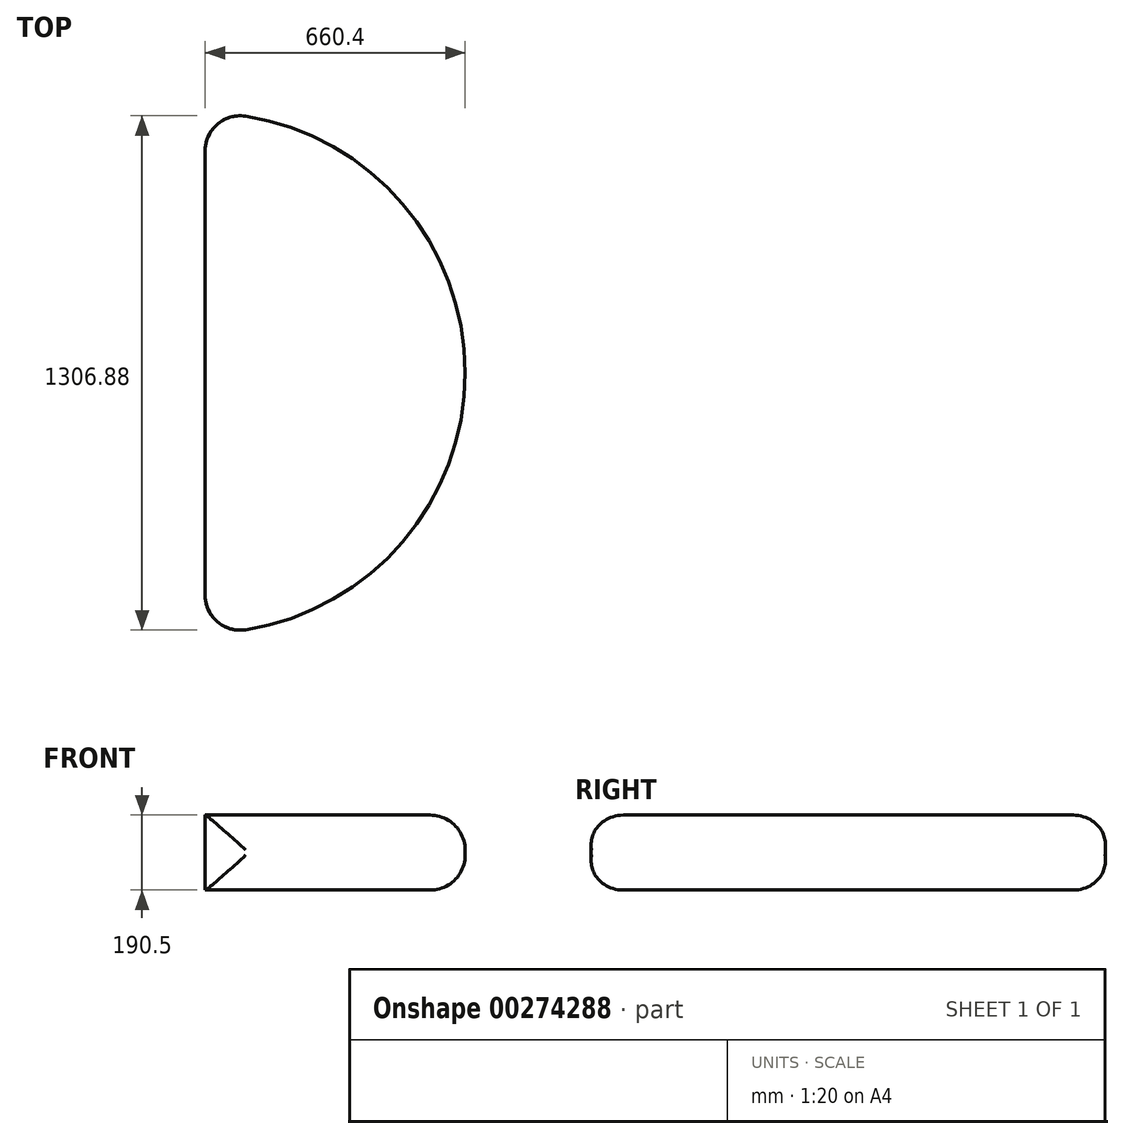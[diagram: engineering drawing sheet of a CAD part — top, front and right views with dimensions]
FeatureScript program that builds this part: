
annotation { "Feature Type Name" : "Feature", "Feature Type Description" : "" }
export const myFeature = defineFeature(function(context is Context, id is Id, definition is map)
    precondition{}
    {
        {
            var Q0;
            Q0=qCreatedBy(makeId("Top.planeOp"),FACE);
            var sketch = newSketch(context, id + "F0", { "sketchPlane" : qUnion([Q0])});
            skLineSegment(sketch, "E0", {"start": v(0, 0) * mm, "end": v(0, 660.4) * mm});
            skArc(sketch, "E1", {"start": v(0, 660.4) * mm, "mid": v(660.4, 0) * mm, "end": v(0, -660.4) * mm});
            skLineSegment(sketch, "E2", {"start": v(0, 0) * mm, "end": v(0, -660.4) * mm});
            skSolve(sketch);
        }
        {
            var Q0;
            Q0 = qSketchRegion(id + "F0", true);
            extrude(context, id + "F1", {"entities" : qUnion([Q0]), "depth" : 190.5 * mm});
        }
        {
            var Q0;
            Q0=makeQuery(id+"F1.opExtrude","SWEPT_FACE",FACE,{"disambiguationData":[OSD([sQuery(id+"F0.wireOp",EDGE,"E1")])]});
            fillet(context, id + "F2", {"entities" : qUnion([Q0]), "radius" : 88.9 * mm, "tangentPropagation" : true, "allowEdgeOverflow" : false});
        }
    });
